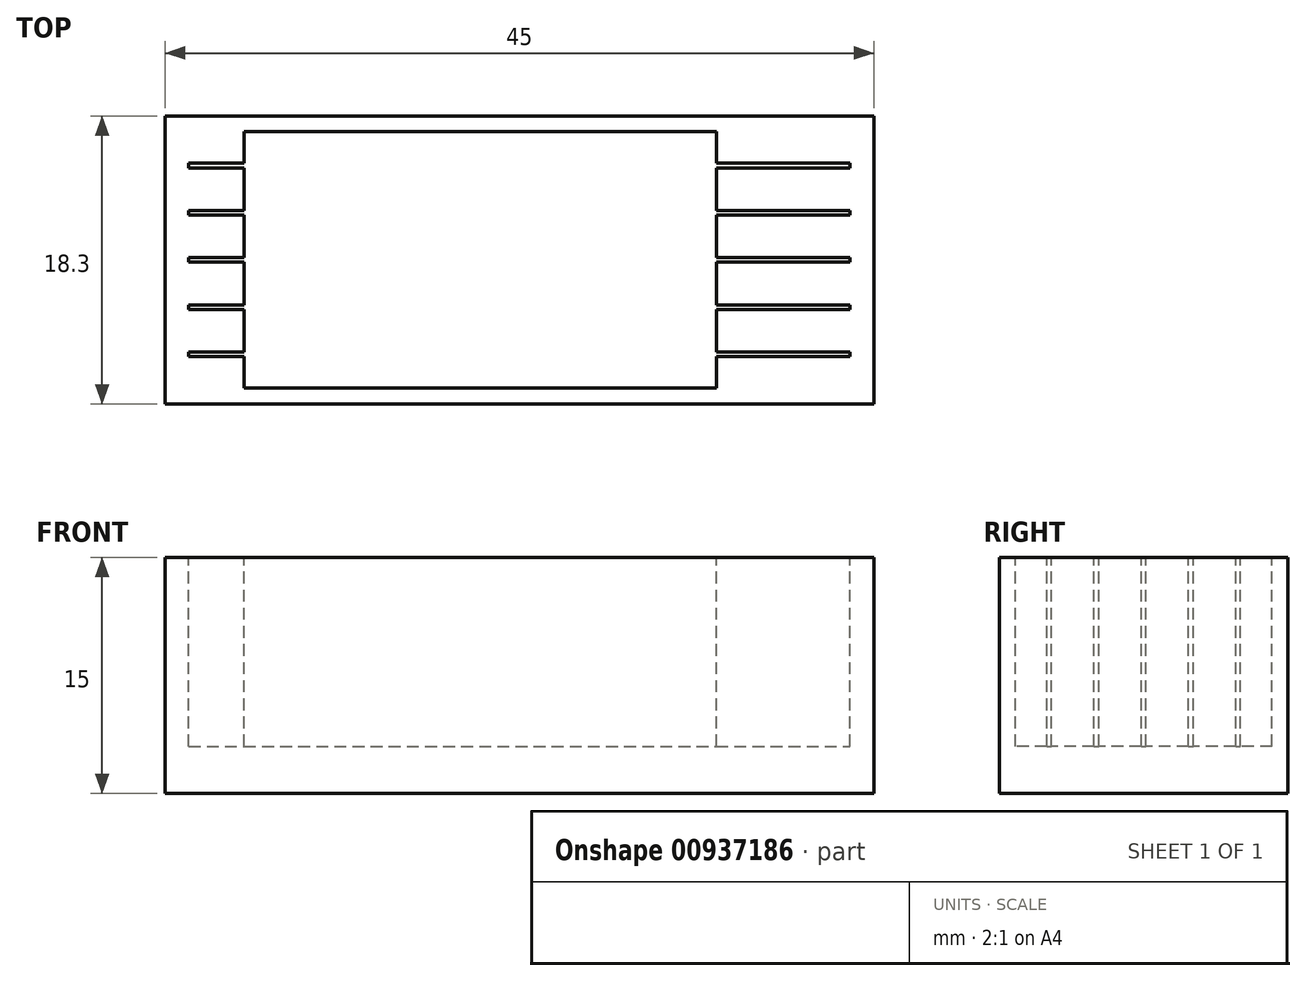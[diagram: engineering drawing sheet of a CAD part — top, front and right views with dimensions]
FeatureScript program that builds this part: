
annotation { "Feature Type Name" : "Feature", "Feature Type Description" : "" }
export const myFeature = defineFeature(function(context is Context, id is Id, definition is map)
    precondition{}
    {
        {
            var Q0;
            Q0=qCreatedBy(makeId("Top.planeOp"),FACE);
            var sketch = newSketch(context, id + "F0", { "sketchPlane" : qUnion([Q0])});
            skLineSegment(sketch, "E0.bottom", {"start": v(-22.5, -8.15) * mm, "end": v(22.5, -8.15) * mm});
            skLineSegment(sketch, "E0.top", {"start": v(-22.5, 8.15) * mm, "end": v(22.5, 8.15) * mm});
            skLineSegment(sketch, "E0.left", {"start": v(-22.5, -8.15) * mm, "end": v(-22.5, 8.15) * mm});
            skLineSegment(sketch, "E0.right", {"start": v(22.5, -8.15) * mm, "end": v(22.5, 8.15) * mm});
            skPoint(sketch, "E0.middle", {"position": v(0, 0) * mm});
            skSolve(sketch);
        }
        {
            var Q0;
            Q0 = qSketchRegion(id + "F0", true);
            extrude(context, id + "F1", {"entities" : qUnion([Q0]), "depth" : 15 * mm, "offsetDistance" : 25 * mm});
        }
        {
            var Q0;
            Q0=makeQuery(id+"F1.opExtrude","CAP_FACE",FACE,{"disambiguationData":[OSD([sQuery(id+"F0.wireOp",EDGE,"E0.bottom"),sQuery(id+"F0.wireOp",EDGE,"E0.top"),sQuery(id+"F0.wireOp",EDGE,"E0.left"),sQuery(id+"F0.wireOp",EDGE,"E0.right")])],"isStart":false});
            var sketch = newSketch(context, id + "F2", { "sketchPlane" : qUnion([Q0])});
            skLineSegment(sketch, "E1.bottom", {"start": v(-21, -6.15) * mm, "end": v(-17.5, -6.15) * mm});
            skLineSegment(sketch, "E1.top", {"start": v(-21, -5.85) * mm, "end": v(-17.5, -5.85) * mm});
            skLineSegment(sketch, "E1.left", {"start": v(-21, -6.15) * mm, "end": v(-21, -5.85) * mm});
            skLineSegment(sketch, "E1.right", {"start": v(21, -6.15) * mm, "end": v(21, -5.85) * mm});
            skPoint(sketch, "E1.middle", {"position": v(0, -6) * mm});
            skLineSegment(sketch, "E2.0.1.0", {"start": v(-21, -3.15) * mm, "end": v(-17.5, -3.15) * mm});
            skLineSegment(sketch, "E2.0.1.1", {"start": v(-21, -2.85) * mm, "end": v(-17.5, -2.85) * mm});
            skPoint(sketch, "E2.0.1.2", {"position": v(0, -3) * mm});
            skLineSegment(sketch, "E2.0.1.3", {"start": v(21, -3.15) * mm, "end": v(21, -2.85) * mm});
            skLineSegment(sketch, "E2.0.1.4", {"start": v(-21, -3.15) * mm, "end": v(-21, -2.85) * mm});
            skLineSegment(sketch, "E2.0.2.0", {"start": v(-21, -0.15) * mm, "end": v(-17.5, -0.15) * mm});
            skLineSegment(sketch, "E2.0.2.1", {"start": v(-21, 0.15) * mm, "end": v(-17.5, 0.15) * mm});
            skPoint(sketch, "E2.0.2.2", {"position": v(0, 0) * mm});
            skLineSegment(sketch, "E2.0.2.3", {"start": v(21, -0.15) * mm, "end": v(21, 0.15) * mm});
            skLineSegment(sketch, "E2.0.2.4", {"start": v(-21, -0.15) * mm, "end": v(-21, 0.15) * mm});
            skLineSegment(sketch, "E2.0.3.0", {"start": v(-21, 2.85) * mm, "end": v(-17.5, 2.85) * mm});
            skLineSegment(sketch, "E2.0.3.1", {"start": v(-21, 3.15) * mm, "end": v(-17.5, 3.15) * mm});
            skPoint(sketch, "E2.0.3.2", {"position": v(0, 3) * mm});
            skLineSegment(sketch, "E2.0.3.3", {"start": v(21, 2.85) * mm, "end": v(21, 3.15) * mm});
            skLineSegment(sketch, "E2.0.3.4", {"start": v(-21, 2.85) * mm, "end": v(-21, 3.15) * mm});
            skLineSegment(sketch, "E2.0.4.0", {"start": v(-21, 5.85) * mm, "end": v(-17.5, 5.85) * mm});
            skLineSegment(sketch, "E2.0.4.1", {"start": v(-21, 6.15) * mm, "end": v(-17.5, 6.15) * mm});
            skPoint(sketch, "E2.0.4.2", {"position": v(0, 6) * mm});
            skLineSegment(sketch, "E2.0.4.3", {"start": v(21, 5.85) * mm, "end": v(21, 6.15) * mm});
            skLineSegment(sketch, "E2.0.4.4", {"start": v(-21, 5.85) * mm, "end": v(-21, 6.15) * mm});
            skLineSegment(sketch, "E2.direction1", {"start": v(-21, -6.15) * mm, "end": v(-17.5, -6.15) * mm, "construction": true});
            skLineSegment(sketch, "E2.direction2", {"start": v(-21, -6.15) * mm, "end": v(-21, -3.15) * mm, "construction": true});
            skLineSegment(sketch, "E3", {"start": v(-17.5, 8.15) * mm, "end": v(-17.5, 6.15) * mm});
            skLineSegment(sketch, "E4", {"start": v(12.5, 8.15) * mm, "end": v(12.5, 6.15) * mm});
            skLineSegment(sketch, "E5.trimOffspring", {"start": v(12.5, 6.15) * mm, "end": v(21, 6.15) * mm});
            skLineSegment(sketch, "E6.trimOffspring", {"start": v(12.5, 5.85) * mm, "end": v(21, 5.85) * mm});
            skLineSegment(sketch, "E7.trimOffspring", {"start": v(12.5, 3.15) * mm, "end": v(21, 3.15) * mm});
            skLineSegment(sketch, "E8.trimOffspring", {"start": v(12.5, 2.85) * mm, "end": v(21, 2.85) * mm});
            skLineSegment(sketch, "E9.trimOffspring", {"start": v(12.5, 0.15) * mm, "end": v(21, 0.15) * mm});
            skLineSegment(sketch, "E10.trimOffspring", {"start": v(12.5, -0.15) * mm, "end": v(21, -0.15) * mm});
            skLineSegment(sketch, "E11.trimOffspring", {"start": v(12.5, -2.85) * mm, "end": v(21, -2.85) * mm});
            skLineSegment(sketch, "E12.trimOffspring", {"start": v(12.5, -3.15) * mm, "end": v(21, -3.15) * mm});
            skLineSegment(sketch, "E13.trimOffspring", {"start": v(12.5, -5.85) * mm, "end": v(21, -5.85) * mm});
            skLineSegment(sketch, "E14.trimOffspring", {"start": v(12.5, -6.15) * mm, "end": v(21, -6.15) * mm});
            skLineSegment(sketch, "E15.trimOffspring", {"start": v(-17.5, 5.85) * mm, "end": v(-17.5, 3.15) * mm});
            skLineSegment(sketch, "E16.trimOffspring", {"start": v(-17.5, 2.85) * mm, "end": v(-17.5, 0.15) * mm});
            skLineSegment(sketch, "E17.trimOffspring", {"start": v(-17.5, -0.15) * mm, "end": v(-17.5, -2.85) * mm});
            skLineSegment(sketch, "E18.trimOffspring", {"start": v(-17.5, -3.15) * mm, "end": v(-17.5, -5.85) * mm});
            skLineSegment(sketch, "E19.trimOffspring", {"start": v(-17.5, -6.15) * mm, "end": v(-17.5, -8.15) * mm});
            skLineSegment(sketch, "E20.trimOffspring", {"start": v(12.5, 5.85) * mm, "end": v(12.5, 3.15) * mm});
            skLineSegment(sketch, "E21.trimOffspring", {"start": v(12.5, 2.85) * mm, "end": v(12.5, 0.15) * mm});
            skLineSegment(sketch, "E22.trimOffspring", {"start": v(12.5, -0.15) * mm, "end": v(12.5, -2.85) * mm});
            skLineSegment(sketch, "E23.trimOffspring", {"start": v(12.5, -3.15) * mm, "end": v(12.5, -5.85) * mm});
            skLineSegment(sketch, "E24.trimOffspring", {"start": v(12.5, -6.15) * mm, "end": v(12.5, -8.15) * mm});
            skLineSegment(sketch, "E25.0", {"start": v(-22.5, 8.15) * mm, "end": v(22.5, 8.15) * mm});
            skLineSegment(sketch, "E26.0.0", {"start": v(12.5, 8.15) * mm, "end": v(-17.5, 8.15) * mm});
            skLineSegment(sketch, "E26.0.1", {"start": v(-22.5, 8.15) * mm, "end": v(-22.5, -8.15) * mm});
            skLineSegment(sketch, "E26.0.2", {"start": v(-17.5, -8.15) * mm, "end": v(12.5, -8.15) * mm});
            skLineSegment(sketch, "E26.0.3", {"start": v(22.5, -8.15) * mm, "end": v(22.5, 8.15) * mm});
            skSolve(sketch);
        }
        {
            var Q0;
            Q0 = qSketchRegion(id + "F2", true);
            extrude(context, id + "F3", {"entities" : qUnion([Q0]), "operationType" : NewBodyOperationType.REMOVE, "oppositeDirection" : true, "depth" : 12 * mm, "offsetDistance" : 25 * mm});
        }
        {
            var Q0;
            Q0=makeQuery(id+"F1.opExtrude","SWEPT_FACE",FACE,{"disambiguationData":[OSD([sQuery(id+"F0.wireOp",EDGE,"E0.bottom")])]});
            var sketch = newSketch(context, id + "F4", { "sketchPlane" : qUnion([Q0])});
            skLineSegment(sketch, "E27.bottom", {"start": v(-22.5, 15) * mm, "end": v(22.5, 15) * mm});
            skLineSegment(sketch, "E27.top", {"start": v(-22.5, 0) * mm, "end": v(22.5, 0) * mm});
            skLineSegment(sketch, "E27.left", {"start": v(-22.5, 15) * mm, "end": v(-22.5, 0) * mm});
            skLineSegment(sketch, "E27.right", {"start": v(22.5, 15) * mm, "end": v(22.5, 0) * mm});
            skSolve(sketch);
        }
        {
            var Q0;
            Q0 = qSketchRegion(id + "F4", true);
            extrude(context, id + "F5", {"entities" : qUnion([Q0]), "operationType" : NewBodyOperationType.ADD, "depth" : 1 * mm, "offsetDistance" : 25 * mm});
        }
        {
            var Q0;
            Q0=makeQuery(id+"F1.opExtrude","SWEPT_FACE",FACE,{"disambiguationData":[OSD([sQuery(id+"F0.wireOp",EDGE,"E0.top")])]});
            var sketch = newSketch(context, id + "F6", { "sketchPlane" : qUnion([Q0])});
            skLineSegment(sketch, "E28.bottom", {"start": v(-22.5, 15) * mm, "end": v(22.5, 15) * mm});
            skLineSegment(sketch, "E28.top", {"start": v(-22.5, 0) * mm, "end": v(22.5, 0) * mm});
            skLineSegment(sketch, "E28.left", {"start": v(-22.5, 15) * mm, "end": v(-22.5, 0) * mm});
            skLineSegment(sketch, "E28.right", {"start": v(22.5, 15) * mm, "end": v(22.5, 0) * mm});
            skSolve(sketch);
        }
        {
            var Q0;
            Q0 = qSketchRegion(id + "F6", true);
            extrude(context, id + "F7", {"entities" : qUnion([Q0]), "operationType" : NewBodyOperationType.ADD, "depth" : 1 * mm, "offsetDistance" : 25 * mm});
        }
    });
